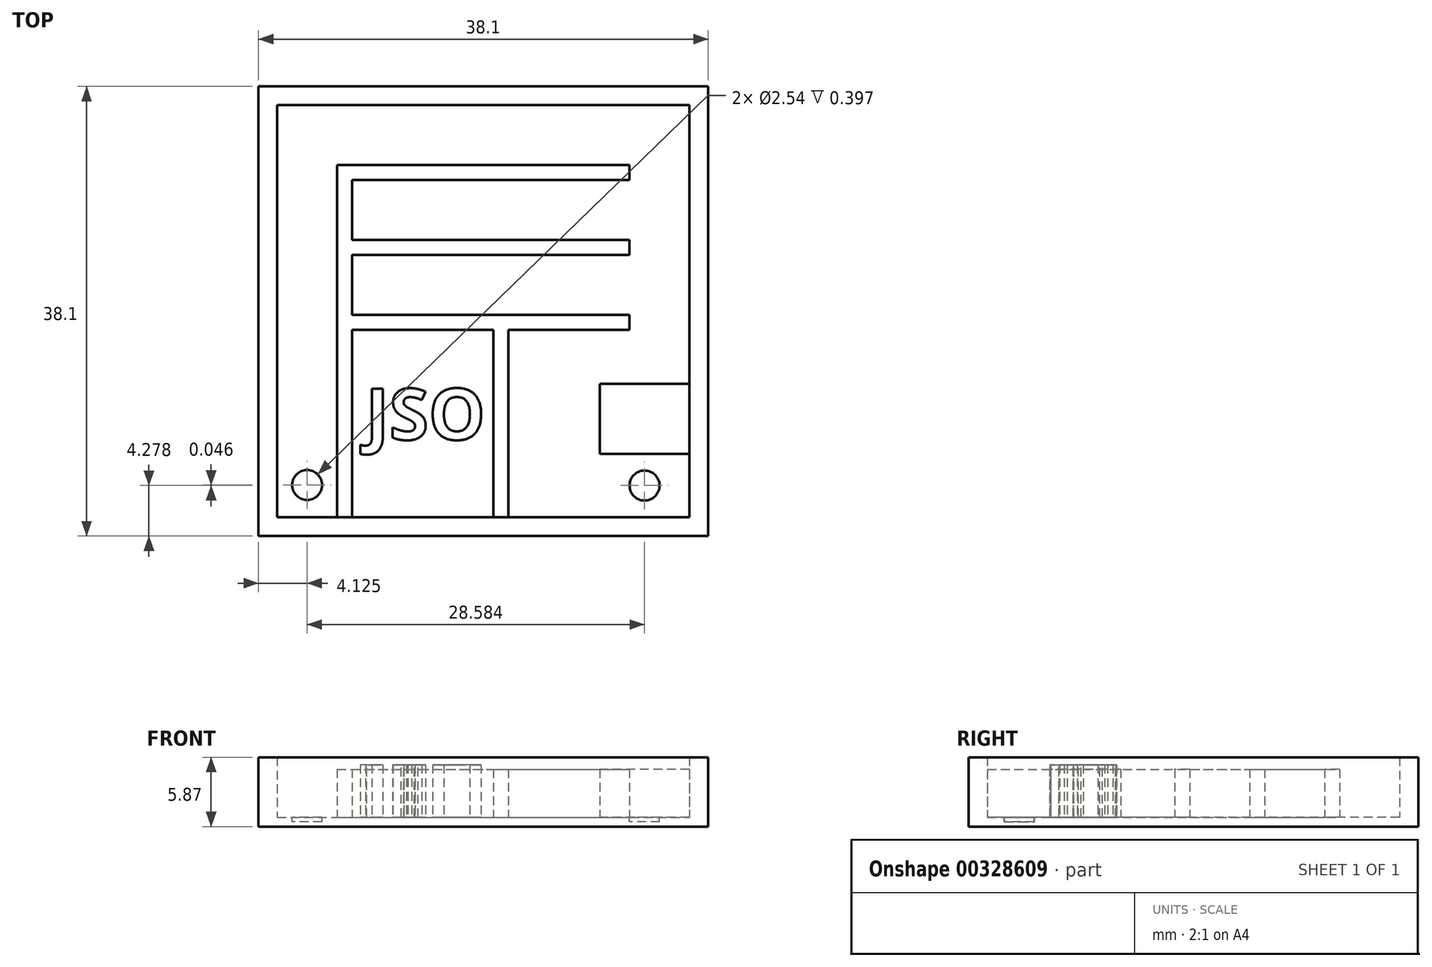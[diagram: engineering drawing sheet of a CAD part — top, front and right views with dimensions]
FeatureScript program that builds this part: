
annotation { "Feature Type Name" : "Feature", "Feature Type Description" : "" }
export const myFeature = defineFeature(function(context is Context, id is Id, definition is map)
    precondition{}
    {
        {
            var Q0;
            Q0=qCreatedBy(makeId("Top.planeOp"),FACE);
            var sketch = newSketch(context, id + "F0", { "sketchPlane" : qUnion([Q0])});
            skLineSegment(sketch, "E0.bottom", {"start": v(-24, 27.21) * mm, "end": v(14.1, 27.21) * mm});
            skLineSegment(sketch, "E0.top", {"start": v(-24, -10.89) * mm, "end": v(14.1, -10.89) * mm});
            skLineSegment(sketch, "E0.left", {"start": v(-24, 27.21) * mm, "end": v(-24, -10.89) * mm});
            skLineSegment(sketch, "E0.right", {"start": v(14.1, 27.21) * mm, "end": v(14.1, -10.89) * mm});
            skSolve(sketch);
        }
        {
            var Q0;
            Q0=makeQuery(id+"F0.imprint","IMPRINT",FACE,{"disambiguationData":[TD([[makeQuery(id+"F0.imprint","IMPRINT",EDGE,{"derivedFrom":sQuery(id+"F0.wireOp",EDGE,"E0.bottom")}),-1.0]])]});
            extrude(context, id + "F1", {"entities" : qUnion([Q0]), "depth" : 0.8 * mm});
        }
        {
            var Q0;
            Q0=makeQuery(id+"F1.opExtrude","CAP_FACE",FACE,{"disambiguationData":[OSD([sQuery(id+"F0.wireOp",EDGE,"E0.bottom"),sQuery(id+"F0.wireOp",EDGE,"E0.top"),sQuery(id+"F0.wireOp",EDGE,"E0.left"),sQuery(id+"F0.wireOp",EDGE,"E0.right")])],"isStart":false});
            var sketch = newSketch(context, id + "F2", { "sketchPlane" : qUnion([Q0])});
            skLineSegment(sketch, "E1.0", {"start": v(-22.41, 25.62) * mm, "end": v(12.51, 25.62) * mm});
            skLineSegment(sketch, "E1.1", {"start": v(-22.41, 25.62) * mm, "end": v(-22.41, -9.3) * mm});
            skLineSegment(sketch, "E1.2", {"start": v(-22.41, -9.3) * mm, "end": v(12.51, -9.3) * mm});
            skLineSegment(sketch, "E1.3", {"start": v(12.51, 25.62) * mm, "end": v(12.51, -9.3) * mm});
            skSolve(sketch);
        }
        {
            var Q0;
            Q0=makeQuery(id+"F2.imprint","IMPRINT",FACE,{"disambiguationData":[TD([[makeQuery(id+"F2.imprint","IMPRINT",EDGE,{"derivedFrom":sQuery(id+"F2.wireOp",EDGE,"E1.0")}),1.0]])]});
            extrude(context, id + "F3", {"entities" : qUnion([Q0]), "operationType" : NewBodyOperationType.ADD, "depth" : 5.08 * mm});
        }
        {
            var Q0;
            Q0=makeQuery(id+"F1.opExtrude","CAP_FACE",FACE,{"disambiguationData":[OSD([sQuery(id+"F0.wireOp",EDGE,"E0.bottom"),sQuery(id+"F0.wireOp",EDGE,"E0.top"),sQuery(id+"F0.wireOp",EDGE,"E0.left"),sQuery(id+"F0.wireOp",EDGE,"E0.right")])],"isStart":false});
            var sketch = newSketch(context, id + "F4", { "sketchPlane" : qUnion([Q0])});
            skLineSegment(sketch, "E2.bottom", {"start": v(-17.33, -9.3) * mm, "end": v(-16.06, -9.3) * mm});
            skLineSegment(sketch, "E2.top", {"start": v(-17.33, 20.54) * mm, "end": v(-16.06, 20.54) * mm});
            skLineSegment(sketch, "E2.left", {"start": v(-17.33, -9.3) * mm, "end": v(-17.33, 20.54) * mm});
            skLineSegment(sketch, "E2.right", {"start": v(-16.06, -9.3) * mm, "end": v(-16.06, 6.57) * mm});
            skLineSegment(sketch, "E3.bottom", {"start": v(-16.06, 20.54) * mm, "end": v(7.43, 20.54) * mm});
            skLineSegment(sketch, "E3.top", {"start": v(-16.06, 19.27) * mm, "end": v(7.43, 19.27) * mm});
            skLineSegment(sketch, "E3.right", {"start": v(7.43, 20.54) * mm, "end": v(7.43, 19.27) * mm});
            skLineSegment(sketch, "E4.bottom", {"start": v(-16.06, 12.92) * mm, "end": v(7.43, 12.92) * mm});
            skLineSegment(sketch, "E4.top", {"start": v(-16.06, 14.2) * mm, "end": v(7.43, 14.2) * mm});
            skLineSegment(sketch, "E4.right", {"start": v(7.43, 12.92) * mm, "end": v(7.43, 14.2) * mm});
            skLineSegment(sketch, "E5.bottom", {"start": v(-16.06, 7.84) * mm, "end": v(7.43, 7.84) * mm});
            skLineSegment(sketch, "E5.top", {"start": v(-16.06, 6.57) * mm, "end": v(-4.1, 6.57) * mm});
            skLineSegment(sketch, "E5.right", {"start": v(7.43, 7.84) * mm, "end": v(7.43, 6.57) * mm});
            skLineSegment(sketch, "E6.top", {"start": v(-2.83, -9.3) * mm, "end": v(-4.1, -9.3) * mm});
            skLineSegment(sketch, "E6.left", {"start": v(-2.83, 6.57) * mm, "end": v(-2.83, -9.3) * mm});
            skLineSegment(sketch, "E6.right", {"start": v(-4.1, 6.57) * mm, "end": v(-4.1, -9.3) * mm});
            skLineSegment(sketch, "E7.trimOffspring", {"start": v(-16.06, 20.54) * mm, "end": v(-16.06, 20.54) * mm});
            skLineSegment(sketch, "E8.trimOffspring", {"start": v(-16.06, 14.2) * mm, "end": v(-16.06, 19.27) * mm});
            skLineSegment(sketch, "E9.trimOffspring", {"start": v(-16.06, 7.84) * mm, "end": v(-16.06, 12.92) * mm});
            skLineSegment(sketch, "E10.trimOffspring", {"start": v(-2.83, 6.57) * mm, "end": v(7.43, 6.57) * mm});
            skLineSegment(sketch, "E11.bottom", {"start": v(3.7, 2.33) * mm, "end": v(7.43, 2.33) * mm});
            skLineSegment(sketch, "E11.top", {"start": v(3.7, -4.58) * mm, "end": v(7.43, -4.58) * mm});
            skLineSegment(sketch, "E11.left", {"start": v(3.7, 2.33) * mm, "end": v(3.7, -4.58) * mm});
            skLineSegment(sketch, "E11.right", {"start": v(7.43, 2.33) * mm, "end": v(7.43, -4.58) * mm});
            skSolve(sketch);
        }
        {
            var Q0;
            Q0=makeQuery(id+"F4.imprint","IMPRINT",FACE,{"disambiguationData":[TD([[makeQuery(id+"F4.imprint","IMPRINT",EDGE,{"derivedFrom":sQuery(id+"F4.wireOp",EDGE,"E2.bottom")}),1.0]])]});
            extrude(context, id + "F5", {"entities" : qUnion([Q0]), "operationType" : NewBodyOperationType.ADD, "depth" : 4.06 * mm});
        }
        {
            var Q0;
            Q0=makeQuery(id+"F5.boolean.opBoolean","SPLIT",FACE,{"disambiguationData":[TD([makeQuery(id+"F3.opExtrude","SWEPT_FACE",FACE,{"disambiguationData":[OSD([sQuery(id+"F2.wireOp",EDGE,"E1.0")])]})])],"derivedFrom":makeQuery(id+"F1.opExtrude","CAP_FACE",FACE,{"disambiguationData":[OSD([sQuery(id+"F0.wireOp",EDGE,"E0.bottom"),sQuery(id+"F0.wireOp",EDGE,"E0.top"),sQuery(id+"F0.wireOp",EDGE,"E0.left"),sQuery(id+"F0.wireOp",EDGE,"E0.right")])],"isStart":false})});
            var sketch = newSketch(context, id + "F6", { "sketchPlane" : qUnion([Q0])});
            skLineSegment(sketch, "E12.bottom", {"start": v(12.51, 2) * mm, "end": v(4.9, 2) * mm});
            skLineSegment(sketch, "E12.top", {"start": v(12.51, -3.92) * mm, "end": v(4.9, -3.92) * mm});
            skLineSegment(sketch, "E12.left", {"start": v(12.51, 2) * mm, "end": v(12.51, -3.92) * mm});
            skLineSegment(sketch, "E12.right", {"start": v(4.9, 2) * mm, "end": v(4.9, -3.92) * mm});
            skSolve(sketch);
        }
        {
            var Q0;
            Q0=makeQuery(id+"F6.imprint","IMPRINT",FACE,{"disambiguationData":[TD([[makeQuery(id+"F6.imprint","IMPRINT",EDGE,{"derivedFrom":sQuery(id+"F6.wireOp",EDGE,"E12.bottom")}),1.0]])]});
            extrude(context, id + "F7", {"entities" : qUnion([Q0]), "operationType" : NewBodyOperationType.ADD, "depth" : 4.06 * mm});
        }
        {
            var Q0;
            Q0=makeQuery(id+"F5.boolean.opBoolean","SPLIT",FACE,{"disambiguationData":[TD([makeQuery(id+"F3.opExtrude","SWEPT_FACE",FACE,{"disambiguationData":[OSD([sQuery(id+"F2.wireOp",EDGE,"E1.0")])]})])],"derivedFrom":makeQuery(id+"F1.opExtrude","CAP_FACE",FACE,{"disambiguationData":[OSD([sQuery(id+"F0.wireOp",EDGE,"E0.bottom"),sQuery(id+"F0.wireOp",EDGE,"E0.top"),sQuery(id+"F0.wireOp",EDGE,"E0.left"),sQuery(id+"F0.wireOp",EDGE,"E0.right")])],"isStart":false})});
            var sketch = newSketch(context, id + "F8", { "sketchPlane" : qUnion([Q0])});
            skLineSegment(sketch, "E13", {"start": v(-22.41, -9.3) * mm, "end": v(-17.33, -9.3) * mm});
            skLineSegment(sketch, "E14", {"start": v(-17.33, -3.83) * mm, "end": v(-17.33, -9.3) * mm});
            skCircle(sketch, "E15", {"center": v(-19.87, -6.57) * mm, "radius": 1.27 * mm});
            skPoint(sketch, "E15.centerSnap0", {"position": v(-17.33, -6.57) * mm});
            skPoint(sketch, "E15.centerSnap1", {"position": v(-19.87, -9.3) * mm});
            skLineSegment(sketch, "E16", {"start": v(4.9, -9.3) * mm, "end": v(12.51, -9.3) * mm});
            skLineSegment(sketch, "E17", {"start": v(12.51, -9.3) * mm, "end": v(12.51, -3.92) * mm});
            skCircle(sketch, "E18", {"center": v(8.7, -6.61) * mm, "radius": 1.27 * mm});
            skPoint(sketch, "E18.centerSnap0", {"position": v(12.51, -6.61) * mm});
            skPoint(sketch, "E18.centerSnap1", {"position": v(8.7, -9.3) * mm});
            skSolve(sketch);
        }
        {
            var Q0;
            Q0=makeQuery(id+"F8.imprint","IMPRINT",FACE,{"disambiguationData":[TD([[makeQuery(id+"F8.imprint","IMPRINT",EDGE,{"derivedFrom":sQuery(id+"F8.wireOp",EDGE,"E15")}),1.0]])]});
            extrude(context, id + "F9", {"entities" : qUnion([Q0]), "operationType" : NewBodyOperationType.REMOVE, "oppositeDirection" : true, "depth" : 0.4 * mm});
        }
        {
            var Q0;
            Q0=makeQuery(id+"F5.boolean.opBoolean","SPLIT",FACE,{"disambiguationData":[TD([makeQuery(id+"F3.opExtrude","SWEPT_FACE",FACE,{"disambiguationData":[OSD([sQuery(id+"F2.wireOp",EDGE,"E1.0")])]})])],"derivedFrom":makeQuery(id+"F1.opExtrude","CAP_FACE",FACE,{"disambiguationData":[OSD([sQuery(id+"F0.wireOp",EDGE,"E0.bottom"),sQuery(id+"F0.wireOp",EDGE,"E0.top"),sQuery(id+"F0.wireOp",EDGE,"E0.left"),sQuery(id+"F0.wireOp",EDGE,"E0.right")])],"isStart":false})});
            var sketch = newSketch(context, id + "F10", { "sketchPlane" : qUnion([Q0])});
            skLineSegment(sketch, "E19", {"start": v(4.9, -9.3) * mm, "end": v(12.51, -9.3) * mm});
            skPoint(sketch, "E19.startSnap0", {"position": v(4.84, -9.3) * mm});
            skLineSegment(sketch, "E20", {"start": v(12.51, -9.3) * mm, "end": v(12.51, -3.92) * mm});
            skCircle(sketch, "E21", {"center": v(8.7, -6.61) * mm, "radius": 1.27 * mm});
            skPoint(sketch, "E21.centerSnap0", {"position": v(12.51, -6.61) * mm});
            skPoint(sketch, "E21.centerSnap1", {"position": v(8.7, -9.3) * mm});
            skSolve(sketch);
        }
        {
            var Q0;
            Q0=makeQuery(id+"F10.imprint","IMPRINT",FACE,{"disambiguationData":[TD([[makeQuery(id+"F10.imprint","IMPRINT",EDGE,{"derivedFrom":sQuery(id+"F10.wireOp",EDGE,"E21")}),1.0]])]});
            extrude(context, id + "F11", {"entities" : qUnion([Q0]), "operationType" : NewBodyOperationType.REMOVE, "oppositeDirection" : true, "depth" : 0.4 * mm});
        }
        {
            var Q0;
            Q0=makeQuery(id+"F5.boolean.opBoolean","SPLIT",FACE,{"disambiguationData":[TD([makeQuery(id+"F5.opExtrude","SWEPT_FACE",FACE,{"disambiguationData":[OSD([sQuery(id+"F4.wireOp",EDGE,"E2.right")])]})])],"derivedFrom":makeQuery(id+"F1.opExtrude","CAP_FACE",FACE,{"disambiguationData":[OSD([sQuery(id+"F0.wireOp",EDGE,"E0.bottom"),sQuery(id+"F0.wireOp",EDGE,"E0.top"),sQuery(id+"F0.wireOp",EDGE,"E0.left"),sQuery(id+"F0.wireOp",EDGE,"E0.right")])],"isStart":false})});
            var sketch = newSketch(context, id + "F12", { "sketchPlane" : qUnion([Q0])});
            skText(sketch, "E22", { "text": "JSO", "fontName": "OpenSans-Bold.ttf"});
            const initialGuessF12  = {"E22": [-0.01492, -0.00273, 1, 0, 0.00435]};
            skSetInitialGuess(sketch, initialGuessF12);
            skSolve(sketch);
        }
        {
            var Q0;
            Q0 = qSketchRegion(id + "F12", true);
            extrude(context, id + "F13", {"entities" : qUnion([Q0]), "operationType" : NewBodyOperationType.ADD, "depth" : 4.44 * mm});
        }
    });
